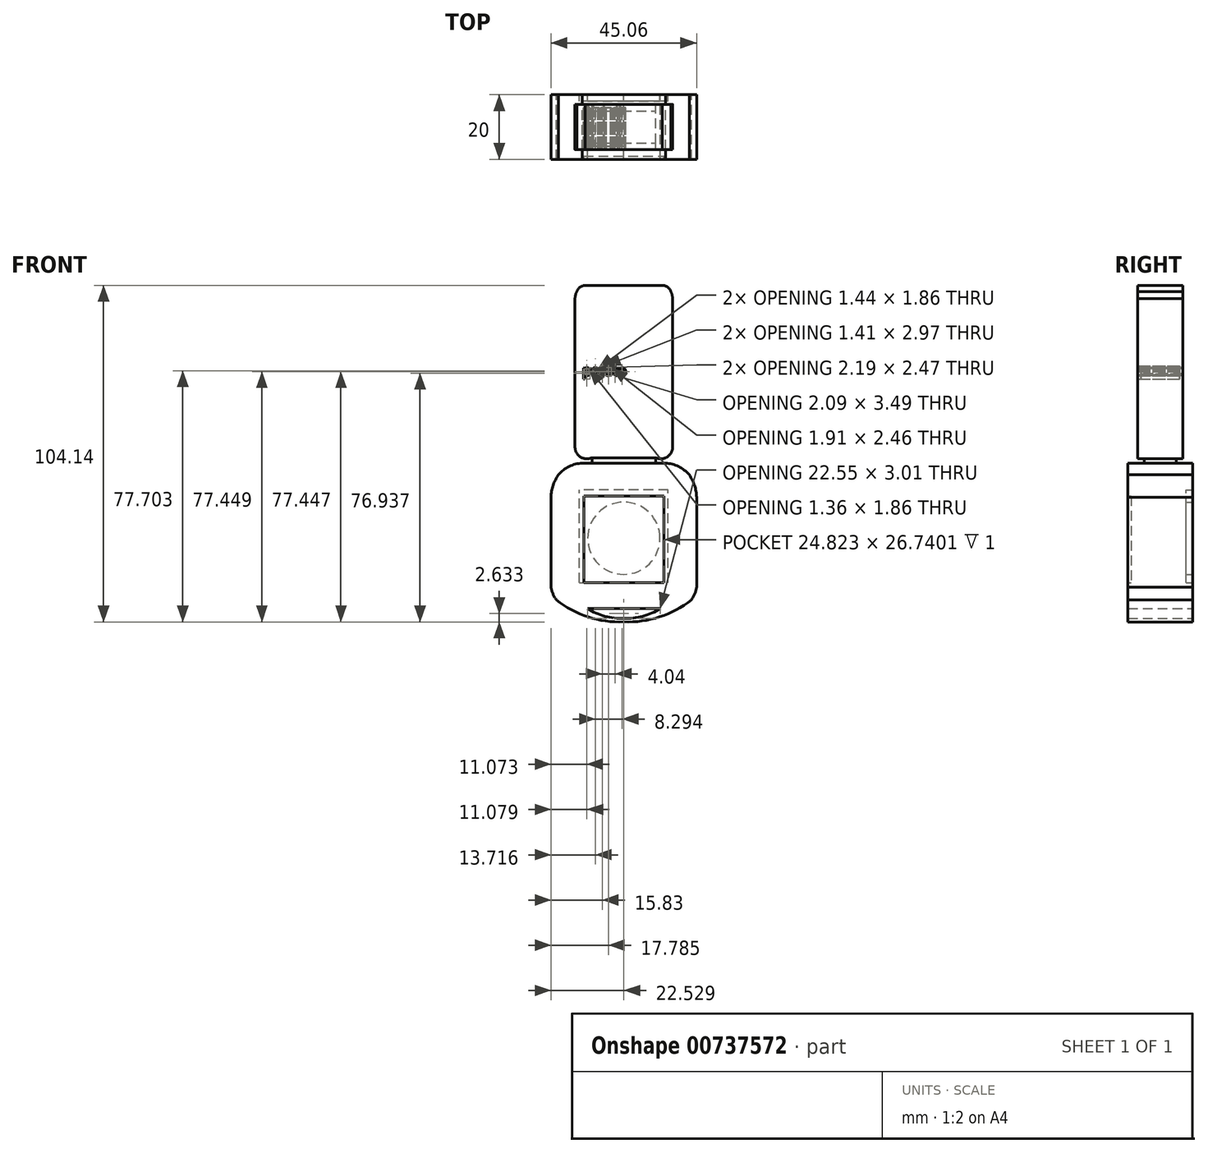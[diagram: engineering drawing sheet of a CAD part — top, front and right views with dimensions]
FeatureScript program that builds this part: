
annotation { "Feature Type Name" : "Feature", "Feature Type Description" : "" }
export const myFeature = defineFeature(function(context is Context, id is Id, definition is map)
    precondition{}
    {
        {
            var Q0;
            Q0=qCreatedBy(makeId("Front.planeOp"),FACE);
            var sketch = newSketch(context, id + "F0", { "sketchPlane" : qUnion([Q0])});
            skLineSegment(sketch, "E0.top", {"start": v(-2.95, 50) * mm, "end": v(-14.9, 50) * mm});
            skLineSegment(sketch, "E0.right", {"start": v(-30, 0) * mm, "end": v(-30, 45.85) * mm});
            skLineSegment(sketch, "E1.top", {"start": v(-24.78, -5) * mm, "end": v(-4.78, -5) * mm});
            skLineSegment(sketch, "E1.left", {"start": v(-24.78, -3.34) * mm, "end": v(-24.78, -5) * mm});
            skLineSegment(sketch, "E2.bottom", {"start": v(-27.78, -5) * mm, "end": v(-2.03, -5) * mm});
            skLineSegment(sketch, "E2.top", {"start": v(-26.18, -50) * mm, "end": v(-3.63, -50) * mm});
            skLineSegment(sketch, "E2.left", {"start": v(-37.43, -15.54) * mm, "end": v(-37.43, -43.38) * mm});
            skLineSegment(sketch, "E2.right", {"start": v(7.63, -15.54) * mm, "end": v(7.63, -43.38) * mm});
            skLineSegment(sketch, "E3.MirrorCS", {"start": v(-26.85, 50) * mm, "end": v(-2.95, 50) * mm});
            skArc(sketch, "E4", {"start": v(-35.12, -8.61) * mm, "mid": v(-36.78, -11.9) * mm, "end": v(-37.43, -15.54) * mm});
            skArc(sketch, "E5", {"start": v(-37.43, -43.38) * mm, "mid": v(-36.84, -45.44) * mm, "end": v(-35.77, -47.3) * mm});
            skArc(sketch, "E6.MirrorCS", {"start": v(5.32, -8.61) * mm, "mid": v(6.98, -11.9) * mm, "end": v(7.63, -15.54) * mm});
            skArc(sketch, "E7.MirrorCS", {"start": v(7.63, -43.38) * mm, "mid": v(7.03, -45.44) * mm, "end": v(5.97, -47.3) * mm});
            skLineSegment(sketch, "E8.MirrorCS", {"start": v(0.2, 0) * mm, "end": v(0.2, 45.85) * mm});
            skPoint(sketch, "E9.MirrorCS.end.orphan", {"position": v(-5.02, -5) * mm});
            skLineSegment(sketch, "E10", {"start": v(0, 0) * mm, "end": v(0.2, 0) * mm});
            skArc(sketch, "E11", {"start": v(-30, 0) * mm, "mid": v(-28.3, -3.1) * mm, "end": v(-24.78, -3.34) * mm});
            skArc(sketch, "E12", {"start": v(-29.47, 48.07) * mm, "mid": v(-29.88, 46.89) * mm, "end": v(-30, 45.63) * mm});
            skArc(sketch, "E13.MirrorCS", {"start": v(-0.34, 48.07) * mm, "mid": v(0.07, 46.89) * mm, "end": v(0.2, 45.63) * mm});
            skArc(sketch, "E14.MirrorCS", {"start": v(0.2, 0) * mm, "mid": v(-1.5, -3.1) * mm, "end": v(-5.02, -3.34) * mm});
            skLineSegment(sketch, "E15.MirrorCS", {"start": v(-5.02, -3.34) * mm, "end": v(-5.02, -5) * mm});
            skPoint(sketch, "E16.orphan", {"position": v(-5.02, 0) * mm});
            skPoint(sketch, "E1.bottom.start.orphan", {"position": v(-24.78, 0) * mm});
            skArc(sketch, "E17", {"start": v(-26.63, 50) * mm, "mid": v(-28.36, 49.5) * mm, "end": v(-29.47, 48.07) * mm});
            skArc(sketch, "E18", {"start": v(-26.85, -5) * mm, "mid": v(-31.4, -5.84) * mm, "end": v(-35.12, -8.61) * mm});
            skLineSegment(sketch, "E19", {"start": v(-14.9, -53) * mm, "end": v(-14.9, -54.1) * mm});
            skArc(sketch, "E20", {"start": v(-35.77, -47.3) * mm, "mid": v(-25.95, -52.58) * mm, "end": v(-14.9, -54.1) * mm});
            skArc(sketch, "E21", {"start": v(-26.18, -50) * mm, "mid": v(-20.77, -52.36) * mm, "end": v(-14.9, -53) * mm});
            skArc(sketch, "E22.MirrorCS", {"start": v(-3.63, -50) * mm, "mid": v(-9.04, -52.36) * mm, "end": v(-14.9, -53) * mm});
            skArc(sketch, "E23.MirrorCS", {"start": v(5.97, -47.3) * mm, "mid": v(-3.85, -52.58) * mm, "end": v(-14.9, -54.1) * mm});
            skArc(sketch, "E24.MirrorCS", {"start": v(-2.95, -5) * mm, "mid": v(1.6, -5.84) * mm, "end": v(5.32, -8.61) * mm});
            skArc(sketch, "E25.MirrorCS", {"start": v(-3.17, 50) * mm, "mid": v(-1.44, 49.5) * mm, "end": v(-0.34, 48.07) * mm});
            skLineSegment(sketch, "E26.bottom", {"start": v(-27.31, -15.21) * mm, "end": v(-2.5, -15.21) * mm});
            skLineSegment(sketch, "E26.top", {"start": v(-27.31, -41.95) * mm, "end": v(-2.5, -41.95) * mm});
            skLineSegment(sketch, "E26.left", {"start": v(-27.31, -15.21) * mm, "end": v(-27.31, -41.95) * mm});
            skLineSegment(sketch, "E26.right", {"start": v(-2.5, -15.21) * mm, "end": v(-2.5, -41.95) * mm});
            skLineSegment(sketch, "E27", {"start": v(-24.78, -3.34) * mm, "end": v(-5.02, -3.34) * mm});
            skText(sketch, "E28", { "text": "potato", "fontName": "OpenSans-Regular.ttf"});
            skLineSegment(sketch, "E29.bottom", {"start": v(-1.2, -41.95) * mm, "end": v(-28.63, -41.95) * mm});
            skLineSegment(sketch, "E29.top", {"start": v(-1.2, -13.22) * mm, "end": v(-28.63, -13.22) * mm});
            skLineSegment(sketch, "E29.left", {"start": v(-1.2, -41.95) * mm, "end": v(-1.2, -13.22) * mm});
            skLineSegment(sketch, "E29.right", {"start": v(-28.63, -41.95) * mm, "end": v(-28.63, -13.22) * mm});
            skCircle(sketch, "E30", {"center": v(-14.89, -28.23) * mm, "radius": 11.17 * mm});
            const initialGuessF0  = {"E28": [-0.02778, 0.02212, 1, 0, 0.0032]};
            skSetInitialGuess(sketch, initialGuessF0);
            skSolve(sketch);
        }
        {
            var Q0;
            {var subQ14=sQuery(id+"F0.wireOp",EDGE,"E11");Q0=makeQuery(id+"F0.imprint","IMPRINT",FACE,{"disambiguationData":[TD([[makeQuery(id+"F0.imprint","IMPRINT",EDGE,{"derivedFrom":subQ14}),1.0]])]});}
            var Q1;
            Q1=makeQuery(id+"F0.imprint","IMPRINT",FACE,{"disambiguationData":[TD([[makeQuery(id+"F0.imprint","IMPRINT",EDGE,{"derivedFrom":sQuery(id+"F0.wireOp",EDGE,"E28.sketch_text.stroke-34")}),1.0]])]});
            var Q2;
            Q2=makeQuery(id+"F0.imprint","IMPRINT",FACE,{"disambiguationData":[TD([[makeQuery(id+"F0.imprint","IMPRINT",EDGE,{"derivedFrom":sQuery(id+"F0.wireOp",EDGE,"E28.sketch_text.stroke-16")}),1.0]])]});
            var Q3;
            Q3=makeQuery(id+"F0.imprint","IMPRINT",FACE,{"disambiguationData":[TD([[makeQuery(id+"F0.imprint","IMPRINT",EDGE,{"derivedFrom":sQuery(id+"F0.wireOp",EDGE,"E28.sketch_text.stroke-80")}),1.0]])]});
            var Q4;
            Q4=makeQuery(id+"F0.imprint","IMPRINT",FACE,{"disambiguationData":[TD([[makeQuery(id+"F0.imprint","IMPRINT",EDGE,{"derivedFrom":sQuery(id+"F0.wireOp",EDGE,"E28.sketch_text.stroke-116")}),1.0]])]});
            extrude(context, id + "F1", {"entities" : qUnion([Q0, Q1, Q2, Q3, Q4]), "depth" : 7 * mm, "offsetDistance" : 25 * mm, "hasSecondDirection" : true, "secondDirectionOppositeDirection" : true, "secondDirectionDepth" : 7 * mm});
        }
        {
            var Q0;
            {var subQ0=sQuery(id+"F0.wireOp",EDGE,"E1.left");Q0=makeQuery(id+"F0.imprint","IMPRINT",FACE,{"disambiguationData":[TD([[makeQuery(id+"F0.imprint","IMPRINT",EDGE,{"derivedFrom":subQ0}),1.0]])]});}
            extrude(context, id + "F2", {"entities" : qUnion([Q0]), "operationType" : NewBodyOperationType.ADD, "depth" : 5 * mm, "offsetDistance" : 25 * mm, "hasSecondDirection" : true, "secondDirectionOppositeDirection" : true, "secondDirectionDepth" : 5 * mm});
        }
        {
            var Q0;
            Q0=makeQuery(id+"F0.imprint","IMPRINT",FACE,{"disambiguationData":[TD([[makeQuery(id+"F0.imprint","IMPRINT",EDGE,{"derivedFrom":sQuery(id+"F0.wireOp",EDGE,"E2.top")}),1.0]])]});
            extrude(context, id + "F3", {"entities" : qUnion([Q0]), "operationType" : NewBodyOperationType.ADD, "depth" : 10 * mm, "offsetDistance" : 25 * mm, "hasSecondDirection" : true, "secondDirectionOppositeDirection" : true, "secondDirectionDepth" : 10 * mm});
        }
        {
            var Q0;
            Q0=makeQuery(id+"F0.imprint","IMPRINT",FACE,{"disambiguationData":[TD([[makeQuery(id+"F0.imprint","IMPRINT",EDGE,{"derivedFrom":sQuery(id+"F0.wireOp",EDGE,"E26.bottom")}),-1.0]])]});
            extrude(context, id + "F4", {"entities" : qUnion([Q0]), "operationType" : NewBodyOperationType.ADD, "depth" : 9 * mm, "offsetDistance" : 25 * mm, "hasSecondDirection" : true, "secondDirectionOppositeDirection" : true, "secondDirectionDepth" : 8 * mm});
        }
        {
            var Q0;
            Q0=makeQuery(id+"F0.imprint","IMPRINT",FACE,{"disambiguationData":[TD([[makeQuery(id+"F0.imprint","IMPRINT",EDGE,{"derivedFrom":sQuery(id+"F0.wireOp",EDGE,"E28.sketch_text.stroke-61")}),-1.0]])]});
            var Q1;
            Q1=makeQuery(id+"F0.imprint","IMPRINT",FACE,{"disambiguationData":[TD([[makeQuery(id+"F0.imprint","IMPRINT",EDGE,{"derivedFrom":sQuery(id+"F0.wireOp",EDGE,"E28.sketch_text.stroke-88")}),-1.0]])]});
            var Q2;
            Q2=makeQuery(id+"F0.imprint","IMPRINT",FACE,{"disambiguationData":[TD([[makeQuery(id+"F0.imprint","IMPRINT",EDGE,{"derivedFrom":sQuery(id+"F0.wireOp",EDGE,"E28.sketch_text.stroke-107")}),-1.0]])]});
            var Q3;
            Q3=makeQuery(id+"F0.imprint","IMPRINT",FACE,{"disambiguationData":[TD([[makeQuery(id+"F0.imprint","IMPRINT",EDGE,{"derivedFrom":sQuery(id+"F0.wireOp",EDGE,"E28.sketch_text.stroke-25")}),-1.0]])]});
            var Q4;
            Q4=makeQuery(id+"F0.imprint","IMPRINT",FACE,{"disambiguationData":[TD([[makeQuery(id+"F0.imprint","IMPRINT",EDGE,{"derivedFrom":sQuery(id+"F0.wireOp",EDGE,"E28.sketch_text.stroke-0")}),-1.0]])]});
            var Q5;
            Q5=makeQuery(id+"F0.imprint","IMPRINT",FACE,{"disambiguationData":[TD([[makeQuery(id+"F0.imprint","IMPRINT",EDGE,{"derivedFrom":sQuery(id+"F0.wireOp",EDGE,"E28.sketch_text.stroke-42")}),-1.0]])]});
            extrude(context, id + "F5", {"entities" : qUnion([Q0, Q1, Q2, Q3, Q4, Q5]), "depth" : 6 * mm, "offsetDistance" : 25 * mm, "hasSecondDirection" : true, "secondDirectionOppositeDirection" : true, "secondDirectionDepth" : 6 * mm});
        }
        {
            var Q0;
            Q0=makeQuery(id+"F0.imprint","IMPRINT",FACE,{"disambiguationData":[TD([[makeQuery(id+"F0.imprint","IMPRINT",EDGE,{"derivedFrom":sQuery(id+"F0.wireOp",EDGE,"E26.bottom")}),1.0]])]});
            extrude(context, id + "F6", {"entities" : qUnion([Q0]), "operationType" : NewBodyOperationType.ADD, "depth" : 10 * mm, "offsetDistance" : 25 * mm, "hasSecondDirection" : true, "secondDirectionOppositeDirection" : true, "secondDirectionDepth" : 8 * mm});
        }
        {
            var Q0;
            Q0=makeQuery(id+"F0.imprint","IMPRINT",FACE,{"disambiguationData":[TD([[makeQuery(id+"F0.imprint","IMPRINT",EDGE,{"derivedFrom":sQuery(id+"F0.wireOp",EDGE,"E30")}),1.0]])]});
            extrude(context, id + "F7", {"entities" : qUnion([Q0]), "operationType" : NewBodyOperationType.ADD, "depth" : 9 * mm, "offsetDistance" : 25 * mm, "hasSecondDirection" : true, "secondDirectionOppositeDirection" : true, "secondDirectionDepth" : 10 * mm});
        }
    });
